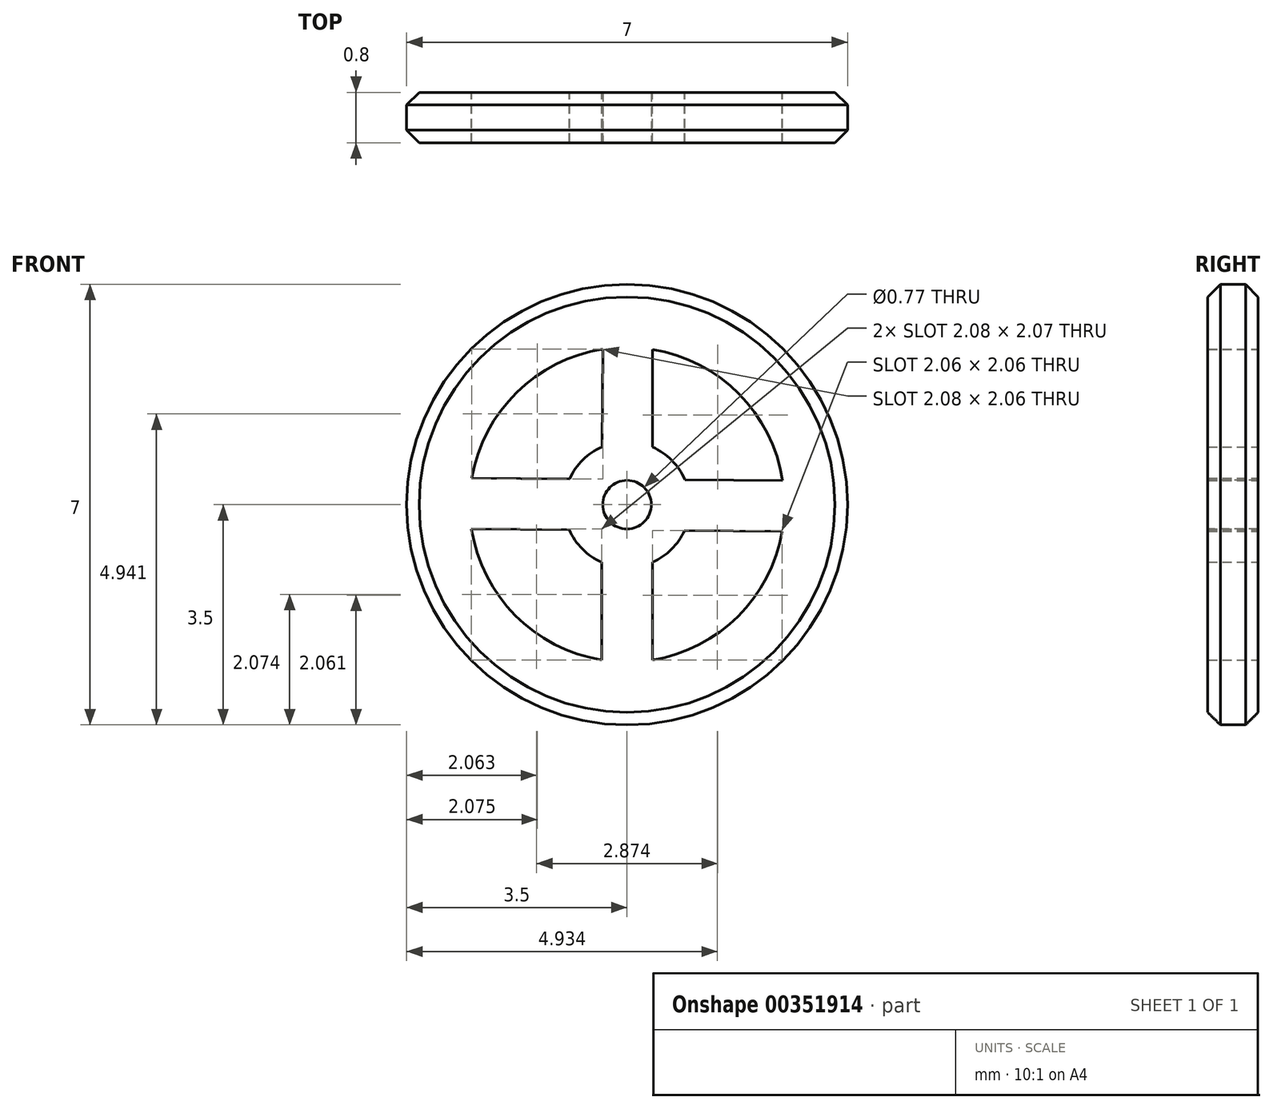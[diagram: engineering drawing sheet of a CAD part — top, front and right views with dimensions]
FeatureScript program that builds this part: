
annotation { "Feature Type Name" : "Feature", "Feature Type Description" : "" }
export const myFeature = defineFeature(function(context is Context, id is Id, definition is map)
    precondition{}
    {
        {
            var Q0;
            Q0=qCreatedBy(makeId("Front.planeOp"),FACE);
            var sketch = newSketch(context, id + "F0", { "sketchPlane" : qUnion([Q0])});
            skCircle(sketch, "E0", {"center": v(0, 0) * mm, "radius": 3.5 * mm});
            skCircle(sketch, "E1", {"center": v(0, 0) * mm, "radius": 2.5 * mm});
            skSolve(sketch);
        }
        {
            var Q0;
            Q0=makeQuery(id+"F0.imprint","IMPRINT",FACE,{"disambiguationData":[TD([[makeQuery(id+"F0.imprint","IMPRINT",EDGE,{"derivedFrom":sQuery(id+"F0.wireOp",EDGE,"E0")}),1.0]])]});
            extrude(context, id + "F1", {"entities" : qUnion([Q0]), "depth" : .8 * mm});
        }
        {
            var Q0;
            Q0=makeQuery(id+"F1.opExtrude","SWEPT_FACE",FACE,{"disambiguationData":[OSD([sQuery(id+"F0.wireOp",EDGE,"E0")])]});
            chamfer(context, id + "F2", {"entities" : qUnion([Q0]), "width" : .2 * mm, "tangentPropagation" : true});
        }
        {
            var Q0;
            Q0=qCreatedBy(makeId("Front.planeOp"),FACE);
            var sketch = newSketch(context, id + "F3", { "sketchPlane" : qUnion([Q0])});
            skLineSegment(sketch, "E2", {"start": v(0.4, -0.91) * mm, "end": v(0.4, -2.47) * mm});
            skLineSegment(sketch, "E3", {"start": v(-0.4, -0.91) * mm, "end": v(-0.4, -2.47) * mm});
            skLineSegment(sketch, "E4", {"start": v(-0.91, 0.41) * mm, "end": v(-2.46, 0.42) * mm});
            skLineSegment(sketch, "E5", {"start": v(-0.92, -0.4) * mm, "end": v(-2.47, -0.38) * mm});
            skLineSegment(sketch, "E6", {"start": v(0.92, 0.4) * mm, "end": v(2.47, 0.38) * mm});
            skLineSegment(sketch, "E7", {"start": v(0.91, -0.41) * mm, "end": v(2.46, -0.42) * mm});
            skLineSegment(sketch, "E8", {"start": v(-0.4, 0.92) * mm, "end": v(-0.38, 2.47) * mm});
            skLineSegment(sketch, "E9", {"start": v(0.4, 0.91) * mm, "end": v(0.4, 2.47) * mm});
            skCircle(sketch, "E10", {"center": v(0, 0) * mm, "radius": 2.5 * mm});
            skArc(sketch, "E11", {"start": v(-0.92, -0.4) * mm, "mid": v(-0.7, -0.7) * mm, "end": v(-0.4, -0.91) * mm});
            skArc(sketch, "E12.trimOffspring", {"start": v(0.4, -0.91) * mm, "mid": v(0.7, -0.7) * mm, "end": v(0.91, -0.41) * mm});
            skArc(sketch, "E13.trimOffspring", {"start": v(0.92, 0.4) * mm, "mid": v(0.7, 0.7) * mm, "end": v(0.4, 0.91) * mm});
            skArc(sketch, "E14.trimOffspring", {"start": v(-0.4, 0.92) * mm, "mid": v(-0.7, 0.71) * mm, "end": v(-0.91, 0.41) * mm});
            skSolve(sketch);
        }
        {
            var Q0;
            {var subQ7=sQuery(id+"F3.wireOp",EDGE,"E2");Q0=makeQuery(id+"F3.imprint","IMPRINT",FACE,{"disambiguationData":[TD([[makeQuery(id+"F3.imprint","IMPRINT",EDGE,{"derivedFrom":subQ7}),-1.0]])]});}
            extrude(context, id + "F4", {"entities" : qUnion([Q0]), "operationType" : NewBodyOperationType.ADD, "depth" : .8 * mm});
        }
        {
            var Q0;
            Q0=makeQuery(id+"F4.boolean.opBoolean","MERGE",FACE,{"derivedFrom":[makeQuery(id+"F1.opExtrude","CAP_FACE",FACE,{"disambiguationData":[OSD([sQuery(id+"F0.wireOp",EDGE,"E0"),sQuery(id+"F0.wireOp",EDGE,"E1")])],"isStart":false}),makeQuery(id+"F4.opExtrude","CAP_FACE",FACE,{"disambiguationData":[OSD([sQuery(id+"F3.wireOp",EDGE,"E2"),sQuery(id+"F3.wireOp",EDGE,"E3"),sQuery(id+"F3.wireOp",EDGE,"E4"),sQuery(id+"F3.wireOp",EDGE,"E5"),sQuery(id+"F3.wireOp",EDGE,"E6"),sQuery(id+"F3.wireOp",EDGE,"E7"),sQuery(id+"F3.wireOp",EDGE,"E8"),sQuery(id+"F3.wireOp",EDGE,"E9"),sQuery(id+"F3.wireOp",EDGE,"E10")])],"isStart":false})]});
            var sketch = newSketch(context, id + "F5", { "sketchPlane" : qUnion([Q0])});
            skCircle(sketch, "E15", {"center": v(0, 0) * mm, "radius": 0.39 * mm});
            skSolve(sketch);
        }
        {
            var Q0;
            Q0=makeQuery(id+"F5.imprint","IMPRINT",FACE,{"disambiguationData":[TD([[makeQuery(id+"F5.imprint","IMPRINT",EDGE,{"derivedFrom":sQuery(id+"F5.wireOp",EDGE,"E15")}),1.0]])]});
            var sketch = newSketch(context, id + "F6", { "sketchPlane" : qUnion([Q0])});
            skCircle(sketch, "E16", {"center": v(0, 0) * mm, "radius": 0.39 * mm});
            skSolve(sketch);
        }
        {
            var Q0;
            Q0 = qSketchRegion(id + "F6", true);
            extrude(context, id + "F7", {"entities" : qUnion([Q0]), "operationType" : NewBodyOperationType.REMOVE, "oppositeDirection" : true, "depth" : 25 * mm});
        }
    });
